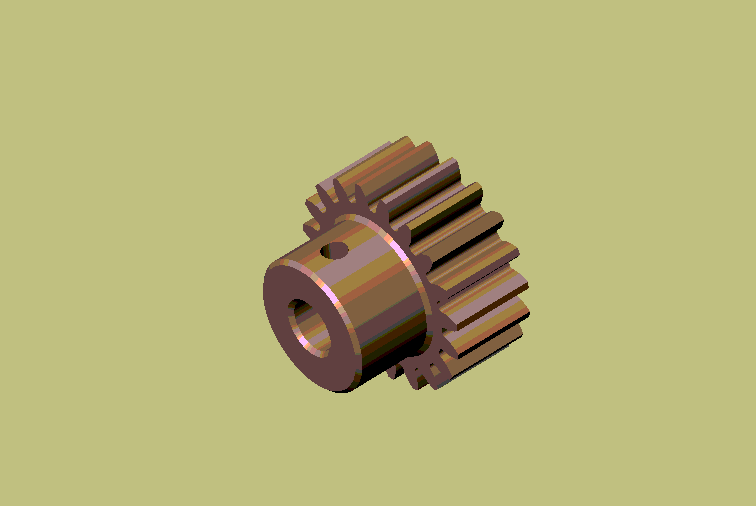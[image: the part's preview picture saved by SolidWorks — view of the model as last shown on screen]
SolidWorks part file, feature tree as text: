
SOLIDWORKS PART (.sldprt)
format: sldprt  version: not decoded by parser v0  size: 441,344 bytes
history: native  units: mm
features: sketch x21, plane x4, chamfer x2, material x1, fillet x1, pattern_circular x1, extrude x1, cut_extrude x1 + 2 further entries (+8 scaffold rows collapsed)
feature tree (42):
  scaffold x8  (default folders/planes/origin — collapsed)
  material  "Matériau <non spécifié>"
  "Corps de surface"
  plane  "Plane1"
  plane  "Plane2"
  plane  "Plane3"
  "Famille de pièces"
  sketch  "Esquisse1"  dims[c1.D2=5.7mm c1.D1=42.0mm c2.D1=~9.473684deg]
  sketch  "Esquisse2"  dims[c1.D2=~5.585416mm c1.D1=37.0mm c2.D1=~10.243359deg]
  sketch  "Esquisse3"  dims[c1.D2=~5.470832mm c1.D1=33.0mm c2.D1=~10.846766deg]
  sketch  "Esquisse4"  dims[c1.D2=~5.356248mm c1.D1=30.0mm c2.D1=~11.181601deg]
  sketch  "Esquisse5"  dims[c1.D2=5.9mm c1.D1=46.0mm c2.D1=~7.836433deg]
  sketch  "Esquisse6"  dims[c1.D2=6.1mm c1.D1=50.0mm c2.D1=~5.91069deg]
  sketch  "Esquisse7"  dims[c1.D2=6.3mm c1.D1=54.0mm c2.D1=~3.757333deg]
  plane  "Plan1"  Offset=5mm
  sketch  "Esquisse8"  dims[c1.D2=5.7mm c1.D1=18.0mm c2.D1=~9.473684deg]
  sketch  "Esquisse9"  dims[c1.D2=~5.585416mm c1.D1=15.0mm c2.D1=~10.243359deg]
  sketch  "Esquisse10"  dims[c1.D2=~5.470832mm c1.D1=13.0mm c2.D1=~10.846766deg]
  sketch  "Esquisse11"  dims[c1.D2=~5.356248mm c1.D1=12.0mm c2.D1=~11.181601deg]
  sketch  "Esquisse12"  dims[c1.D2=5.9mm c1.D1=20.0mm c2.D1=~7.836433deg]
  sketch  "Esquisse13"  dims[c1.D2=6.1mm c1.D1=21.0mm c2.D1=~5.91069deg]
  sketch  "Esquisse14"  dims[c1.D2=6.3mm c1.D1=22.0mm c2.D1=~3.757333deg]
  sketch  "Esquisse15"  dims[c1.D2=4.95mm c1.D1=23.0mm c2.D1=~11.181601deg]
  sketch  "Esquisse16"  dims[c1.D2=4.95mm c1.D1=10.0mm c2.D1=~11.181601deg]
  sketch  "Esquisse17"  dims[D1=9.9mm]
  sketch  "Esquisse18"  dims[D1=9.9mm]
  fillet  "Congé1"  Radius=0.25mm
  pattern_circular  "Répétition circulaire1"  Count=19 Angle=360deg
  sketch  "Esquisse19"  dims[D1=8.0mm]
  extrude  "Boss.-Extru.1"  Depth=5mm
  sketch  "Esquisse20"  dims[D1=~5.192858mm]
  cut_extrude  "Enlèv. mat.-Extru.1"  [1 undecoded]
  chamfer  "Chanfrein1"  Distance=0.25mm Angle=45deg
  sketch  "Esquisse21"  dims[D1=1.5mm]
  chamfer  "Enlèv. mat.-Extru.2"  Distance=35mm
decode coverage: 26 of 27 modeling features carry decoded parameters; 2 rows unclassified (native names shown)
note: ~ marks probable driven/reference dimensions
note: 1 parameter value undecoded
note: suppression state not decoded; provenance and decode notes live in map.json
